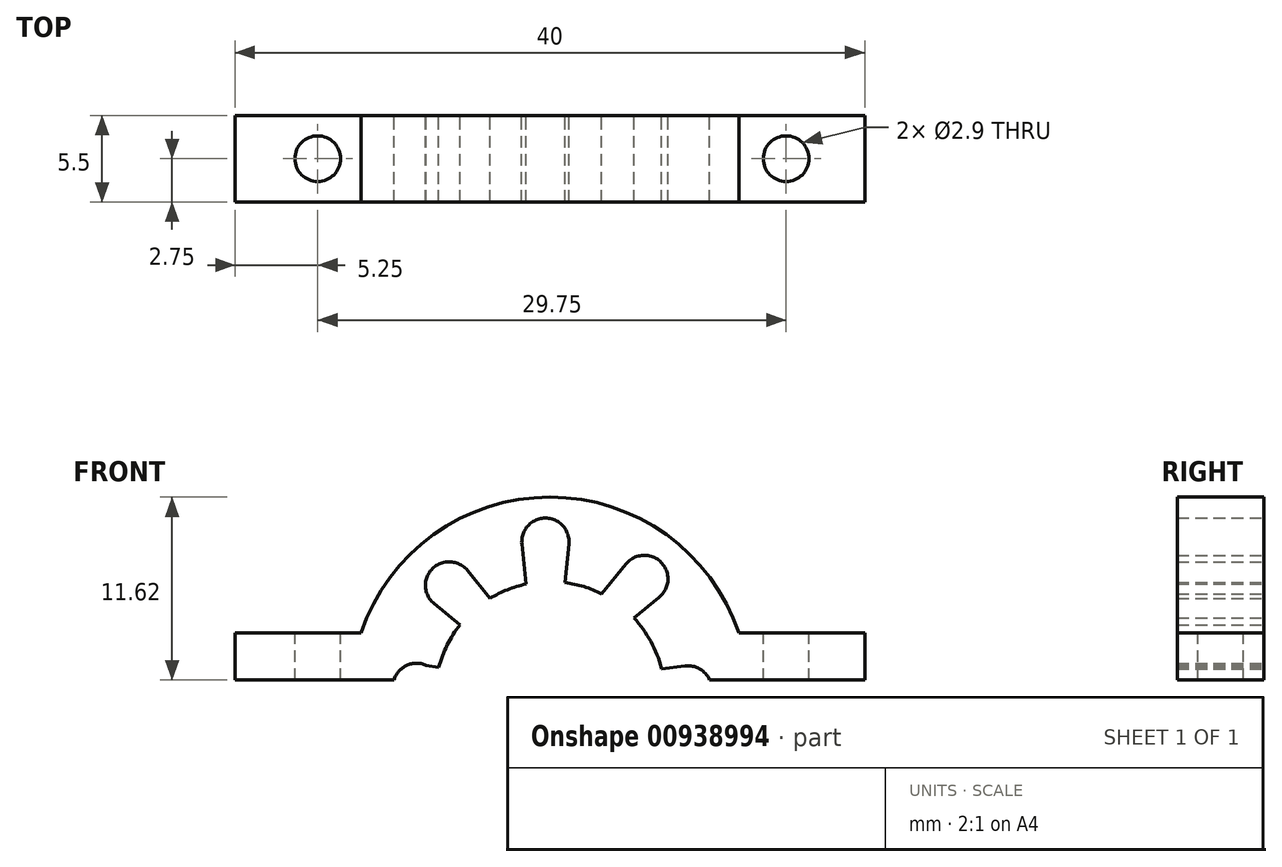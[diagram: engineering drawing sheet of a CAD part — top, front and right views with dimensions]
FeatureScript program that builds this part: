
annotation { "Feature Type Name" : "Feature", "Feature Type Description" : "" }
export const myFeature = defineFeature(function(context is Context, id is Id, definition is map)
    precondition{}
    {
        {
            var Q0;
            Q0=qCreatedBy(makeId("Front.planeOp"),FACE);
            var sketch = newSketch(context, id + "F0", { "sketchPlane" : qUnion([Q0])});
            skLineSegment(sketch, "E0.top", {"start": v(20, -7.75) * mm, "end": v(10, -7.75) * mm});
            skLineSegment(sketch, "E0.left", {"start": v(20, -4.75) * mm, "end": v(20, -7.75) * mm});
            skLineSegment(sketch, "E0.right", {"start": v(-20, -4.75) * mm, "end": v(-20, -7.75) * mm});
            skPoint(sketch, "E0.middle", {"position": v(0, 0) * mm});
            skLineSegment(sketch, "E1.trimOffspring", {"start": v(-10, -7.75) * mm, "end": v(-20, -7.75) * mm});
            skLineSegment(sketch, "E2", {"start": v(-20, -7.75) * mm, "end": v(-20, -4.75) * mm});
            skLineSegment(sketch, "E3", {"start": v(20, -7.75) * mm, "end": v(20, -4.75) * mm});
            skLineSegment(sketch, "E4", {"start": v(20, -4.75) * mm, "end": v(12, -4.75) * mm});
            skLineSegment(sketch, "E5", {"start": v(-20, -4.75) * mm, "end": v(-12, -4.75) * mm});
            skArc(sketch, "E6", {"start": v(12, -4.75) * mm, "mid": v(0, 3.87) * mm, "end": v(-12, -4.75) * mm});
            skPoint(sketch, "E0.bottom.end.orphan", {"position": v(-20, 7.75) * mm});
            skPoint(sketch, "E7.orphan", {"position": v(20, 7.75) * mm});
            skArc(sketch, "E8", {"start": v(3.28, -2.27) * mm, "mid": v(2.15, -1.81) * mm, "end": v(0.96, -1.55) * mm});
            skPoint(sketch, "E9", {"position": v(8.76, -8.33) * mm});
            skPoint(sketch, "E10", {"position": v(-8.47, -8.17) * mm});
            skPoint(sketch, "E11", {"position": v(-0.3, 1.04) * mm});
            skPoint(sketch, "E12", {"position": v(6, -1.32) * mm});
            skPoint(sketch, "E13", {"position": v(-6.4, -1.73) * mm});
            skArc(sketch, "E14", {"start": v(6.94, -2.49) * mm, "mid": v(7.06, -0.26) * mm, "end": v(4.83, -0.37) * mm});
            skArc(sketch, "E15", {"start": v(1.2, 0.9) * mm, "mid": v(-0.3, 2.54) * mm, "end": v(-1.78, 0.9) * mm});
            skArc(sketch, "E16", {"start": v(-5.24, -0.78) * mm, "mid": v(-7.47, -0.67) * mm, "end": v(-7.35, -2.9) * mm});
            skLineSegment(sketch, "E17", {"start": v(6.94, -2.49) * mm, "end": v(5.94, -3.3) * mm});
            skLineSegment(sketch, "E18", {"start": v(4.83, -0.37) * mm, "end": v(3.28, -2.27) * mm});
            skLineSegment(sketch, "E19", {"start": v(1.2, 0.9) * mm, "end": v(0.96, -1.55) * mm});
            skLineSegment(sketch, "E20", {"start": v(-1.78, 0.9) * mm, "end": v(-1.53, -1.65) * mm});
            skLineSegment(sketch, "E21", {"start": v(-5.24, -0.78) * mm, "end": v(-3.8, -2.56) * mm});
            skLineSegment(sketch, "E22", {"start": v(-7.35, -2.9) * mm, "end": v(-5.7, -4.24) * mm});
            skArc(sketch, "E23.trimOffspring", {"start": v(-1.53, -1.65) * mm, "mid": v(-2.7, -2) * mm, "end": v(-3.8, -2.56) * mm});
            skArc(sketch, "E24.trimOffspring", {"start": v(-5.7, -4.24) * mm, "mid": v(-1.55, -15.92) * mm, "end": v(7.08, -7.02) * mm});
            skCircle(sketch, "E25", {"center": v(8.76, -8.33) * mm, "radius": 1.5 * mm});
            skCircle(sketch, "E26", {"center": v(-8.47, -8.17) * mm, "radius": 1.5 * mm});
            skArc(sketch, "E27", {"start": v(3.28, -2.27) * mm, "mid": v(3.5, -4.1) * mm, "end": v(5.33, -3.8) * mm});
            skArc(sketch, "E28", {"start": v(-1.53, -1.65) * mm, "mid": v(-0.2, -3.83) * mm, "end": v(0.96, -1.55) * mm});
            skArc(sketch, "E29", {"start": v(-5.7, -4.24) * mm, "mid": v(-3.52, -4.8) * mm, "end": v(-3.8, -2.56) * mm});
            skLineSegment(sketch, "E30", {"start": v(8.58, -6.84) * mm, "end": v(7.08, -7.02) * mm});
            skLineSegment(sketch, "E31", {"start": v(-8.55, -6.68) * mm, "end": v(-7.06, -6.95) * mm});
            skPoint(sketch, "E32.visualSharp", {"position": v(5.33, -3.8) * mm});
            skLineSegment(sketch, "E33", {"start": v(5.94, -3.3) * mm, "end": v(5.33, -3.8) * mm});
            skCircle(sketch, "E34", {"center": v(0, -8.8) * mm, "radius": 7.3 * mm});
            skLineSegment(sketch, "E35", {"start": v(-10, -7.75) * mm, "end": v(-9.91, -7.75) * mm});
            skLineSegment(sketch, "E36", {"start": v(10.14, -7.75) * mm, "end": v(10, -7.75) * mm});
            skPoint(sketch, "E37.center.orphan", {"position": v(0, -7.75) * mm});
            skSolve(sketch);
        }
        {
            var Q0;
            Q0=makeQuery(id+"F0.imprint","IMPRINT",FACE,{"disambiguationData":[TD([[makeQuery(id+"F0.imprint","IMPRINT",EDGE,{"derivedFrom":sQuery(id+"F0.wireOp",EDGE,"zAmP718W-1A7a-TJuy-Mgxu-dcLFKYdscgSj")}),-1.0]])]});
            var Q1;
            Q1=makeQuery(id+"F0.imprint","IMPRINT",FACE,{"disambiguationData":[TD([[makeQuery(id+"F0.imprint","IMPRINT",EDGE,{"derivedFrom":sQuery(id+"F0.wireOp",EDGE,"E0.top")}),-1.0]])]});
            extrude(context, id + "F1", {"entities" : qUnion([Q0, Q1]), "depth" : 5.5 * mm, "offsetDistance" : 25 * mm});
        }
        {
            var Q0;
            Q0=makeQuery(id+"F1.opExtrude","SWEPT_FACE",FACE,{"disambiguationData":[OSD([sQuery(id+"F0.wireOp",EDGE,"E5")])]});
            var sketch = newSketch(context, id + "F2", { "sketchPlane" : qUnion([Q0])});
            skLineSegment(sketch, "E38", {"start": v(-20, -5.5) * mm, "end": v(-17.5, -5.5) * mm});
            skLineSegment(sketch, "E39", {"start": v(-17.5, -5.5) * mm, "end": v(-17.5, 0) * mm});
            skLineSegment(sketch, "E40", {"start": v(-17.5, -2.75) * mm, "end": v(-12, -2.75) * mm, "construction": true});
            skCircle(sketch, "E41", {"center": v(-14.75, -2.75) * mm, "radius": 1.45 * mm});
            skSolve(sketch);
        }
        {
            var Q0;
            Q0=makeQuery(id+"F2.imprint","IMPRINT",FACE,{"disambiguationData":[TD([[makeQuery(id+"F2.imprint","IMPRINT",EDGE,{"derivedFrom":sQuery(id+"F2.wireOp",EDGE,"E41")}),1.0]])]});
            extrude(context, id + "F3", {"entities" : qUnion([Q0]), "operationType" : NewBodyOperationType.REMOVE, "oppositeDirection" : true, "depth" : 25 * mm, "offsetDistance" : 25 * mm});
        }
        {
            var Q0;
            Q0=makeQuery(id+"F1.opExtrude","SWEPT_FACE",FACE,{"disambiguationData":[OSD([sQuery(id+"F0.wireOp",EDGE,"E4")])]});
            var sketch = newSketch(context, id + "F4", { "sketchPlane" : qUnion([Q0])});
            skLineSegment(sketch, "E42", {"start": v(20, -5.5) * mm, "end": v(18, -5.5) * mm, "construction": true});
            skLineSegment(sketch, "E43", {"start": v(18, 0) * mm, "end": v(18, -5.5) * mm, "construction": true});
            skLineSegment(sketch, "E44", {"start": v(18, -2.75) * mm, "end": v(12, -2.75) * mm, "construction": true});
            skCircle(sketch, "E45", {"center": v(15, -2.75) * mm, "radius": 1.45 * mm});
            skSolve(sketch);
        }
        {
            var Q0;
            Q0=makeQuery(id+"F4.imprint","IMPRINT",FACE,{"disambiguationData":[TD([[makeQuery(id+"F4.imprint","IMPRINT",EDGE,{"derivedFrom":sQuery(id+"F4.wireOp",EDGE,"E45")}),1.0]])]});
            extrude(context, id + "F5", {"entities" : qUnion([Q0]), "operationType" : NewBodyOperationType.REMOVE, "oppositeDirection" : true, "depth" : 25 * mm, "offsetDistance" : 25 * mm});
        }
    });
